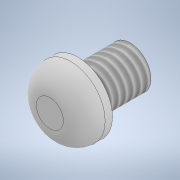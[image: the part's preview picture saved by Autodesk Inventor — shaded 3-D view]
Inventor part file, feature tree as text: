
AUTODESK INVENTOR PART (.ipt)
format: ipt  version: 2021 (Build 250183000, 183)  size: 128,512 bytes
history: native  units: mm
features: extrude x2, sketch x2, fillet x1, thread x1
ambient origin geometry x8: Origin, YZ Plane, XZ Plane, XY Plane, X Axis, Y Axis, Z Axis, Center Point
bodies: Solid1 (feature_tree)
feature tree (6):
  extrude  "Extrusion1"  Depth=2.7mm TaperAngle=0.0deg
  fillet  "Fillet1"  Radius=2.0mm
  extrude  "Extrusion2"  Depth=5.0mm TaperAngle=0.0deg
  thread  "Thread1"  [1 undecoded]
  sketch  "Sketch1"  dims[d0=6.6mm d1=2.7mm d2=0.0mm d3=2.0mm]
  sketch  "Sketch2"  dims[d4=4.0mm d5=5.0mm d6=0.0mm d7=5.0mm d8=0.0mm]
note: 1 required parameter value undecoded (feature->parameter linkage not recoverable at this tier; creation-order binding heuristic only, values carry confidence <= 0.55)
